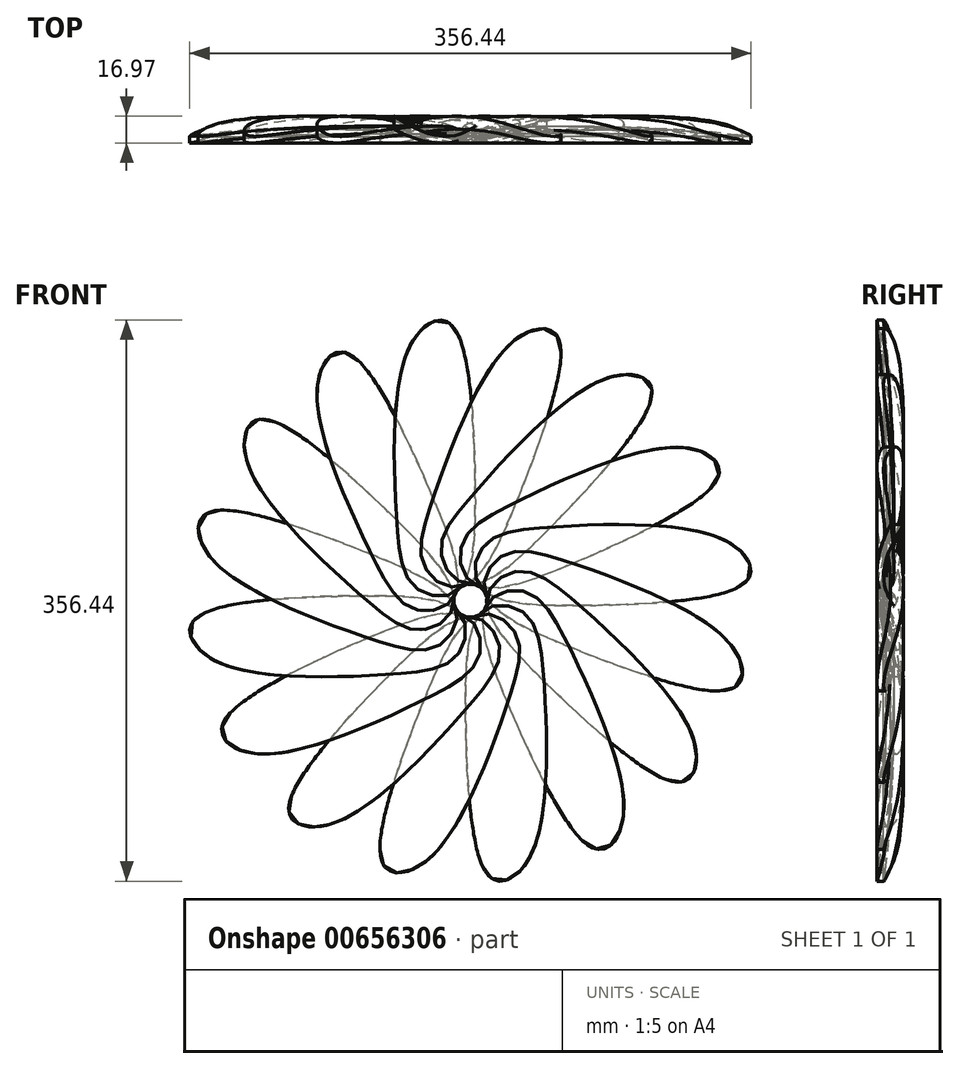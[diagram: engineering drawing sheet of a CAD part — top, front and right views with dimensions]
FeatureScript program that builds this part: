
annotation { "Feature Type Name" : "Feature", "Feature Type Description" : "" }
export const myFeature = defineFeature(function(context is Context, id is Id, definition is map)
    precondition{}
    {
        {
            var Q0;
            Q0=qCreatedBy(makeId("Front.planeOp"),FACE);
            var sketch = newSketch(context, id + "F0", { "sketchPlane" : qUnion([Q0])});
            skFitSpline(sketch, "E0", {"points": [v(-7.45, 168.14) * mm, v(-19.81, 178.2) * mm, v(-40.53, 156.84) * mm, v(-46.6, 49.2) * mm, v(-34.49, 8.14) * mm, v(-9.17, 5.75) * mm, v(3.06, 70.3) * mm, v(-7.45, 168.14) * mm]});
            skSolve(sketch);
        }
        {
            var Q0;
            Q0 = qSketchRegion(id + "F0", true);
            extrude(context, id + "F1", {"entities" : qUnion([Q0]), "oppositeDirection" : true, "depth" : 204 * mm, "offsetDistance" : 25 * mm});
        }
        {
            var Q0;
            Q0=qCreatedBy(makeId("Top.planeOp"),FACE);
            var sketch = newSketch(context, id + "F2", { "sketchPlane" : qUnion([Q0])});
            skFitSpline(sketch, "E1", {"points": [v(39.15, 77.67) * mm, v(-10.96, 31.25) * mm, v(-84.73, 69.57) * mm, v(-84.73, 72.04) * mm, v(-29.46, 37.56) * mm, v(12.52, 49.27) * mm, v(39.15, 77.67) * mm]});
            skSolve(sketch);
        }
        {
            var Q0;
            Q0 = qSketchRegion(id + "F2", true);
            extrude(context, id + "F3", {"entities" : qUnion([Q0]), "operationType" : NewBodyOperationType.INTERSECT, "depth" : 239 * mm, "offsetDistance" : 25 * mm});
        }
        {
            var Q0;
            Q0=qCreatedBy(makeId("Right.planeOp"),FACE);
            var sketch = newSketch(context, id + "F4", { "sketchPlane" : qUnion([Q0])});
            skLineSegment(sketch, "E2", {"start": v(-161.6, 0) * mm, "end": v(193.74, 0) * mm});
            skSolve(sketch);
        }
        {
            var Q0;
            Q0=makeQuery(id+"F1.opExtrude","SWEPT_BODY",BODY,{"disambiguationData":[OSD([sQuery(id+"F0.wireOp",EDGE,"E0")])]});
            var Q1;
            Q1=sQuery(id+"F4.wireOp",EDGE,"E2");
            circularPattern(context, id + "F5", {"entities" : qUnion([Q0]), "axis" : qUnion([Q1]), "angle" : 360 * degree, "instanceCount" : 16, "equalSpace" : true});
        }
    });
